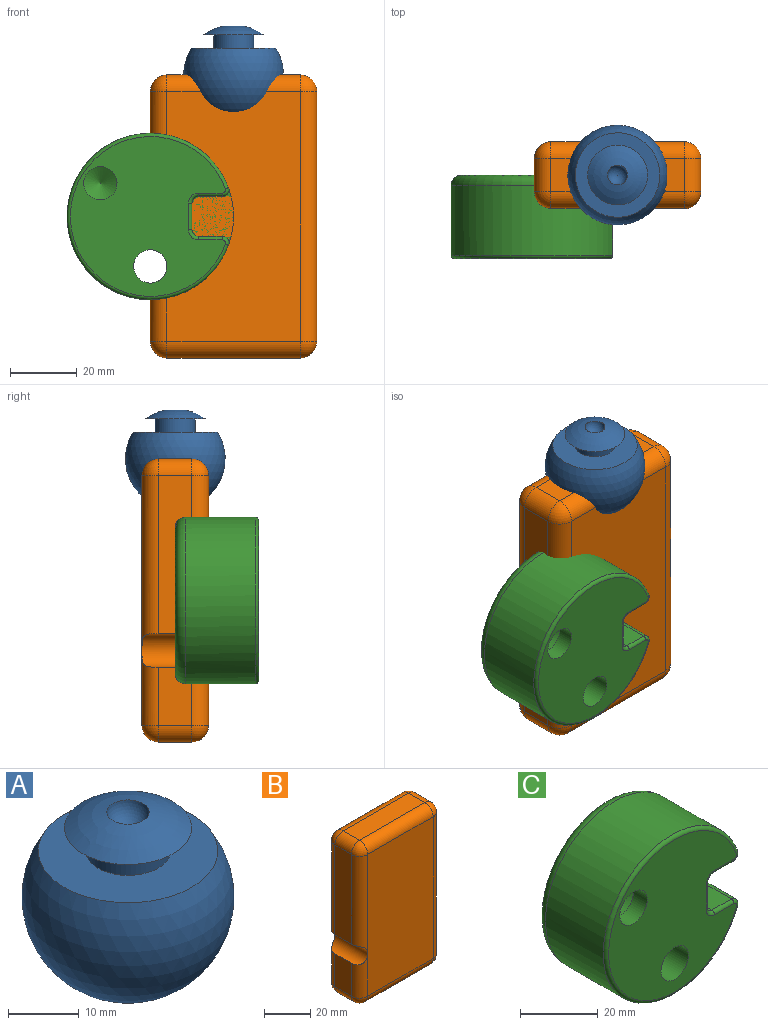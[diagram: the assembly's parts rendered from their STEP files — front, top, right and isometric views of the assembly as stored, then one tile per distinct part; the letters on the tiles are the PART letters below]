
ASSEMBLY  parts=3 mates=2
PART A: 6 faces, bbox 30x30x29.7 mm
  f0: sphere r=15mm, area 254.5mm2, adj f1,f4
  f1: sphere r=3mm, area 50.9mm2, adj f0
  f2: cylinder r=6mm len=12mm, axis (0,0,1), area 150.8mm2, adj f3,f4
  f3: plane 25.38x25.38mm, normal (0,0,1), area 392.7mm2, adj f2,f5
  f4: plane 18x18mm, normal (0,0,-1), area 141.4mm2, adj f0,f2
  f5: sphere r=15mm, area 2167.7mm2, adj f3
PART B: 30 faces, bbox 50x20x85 mm
  f0: plane 47.5x10mm, normal (-1,0,0), area 475mm2, adj f7,f8,f9,f25
  f1: plane 17.5x10mm, normal (-1,0,0), area 175mm2, adj f7,f12,f13,f17
  f2: plane 40x10mm, normal (0,0,-1), area 400mm2, adj f14,f17,f18,f21
  f3: plane 75x40mm, normal (0,1,0), area 3000mm2, adj f8,f10,f12,f21,f29
  f4: plane 40x10mm, normal (0,0,1), area 400mm2, adj f22,f25,f26,f29
  f5: plane 75x40mm, normal (0,-1,0), area 3000mm2, adj f9,f11,f13,f14,f22
  f6: plane 75x10mm, normal (1,0,0), area 750mm2, adj f10,f11,f18,f26
  f7: cylinder r=5mm len=20mm, axis (0,-1,0), area 291.5mm2, adj f0,f1,f8,f9,f12,f13
  f8: cylinder r=5mm len=52.5mm, axis (0,0,-1), area 378.7mm2, adj f0,f3,f7,f27
  f9: cylinder r=5mm len=52.5mm, axis (0,0,1), area 378.7mm2, adj f0,f5,f7,f23
  f10: cylinder r=5mm len=75mm, axis (0,0,1), area 589mm2, adj f3,f6,f20,f28
  f11: cylinder r=5mm len=75mm, axis (0,0,-1), area 589mm2, adj f5,f6,f16,f24
  f12: cylinder r=5mm len=22.5mm, axis (0,0,-1), area 143.1mm2, adj f1,f3,f7,f19
  f13: cylinder r=5mm len=22.5mm, axis (0,0,1), area 143.1mm2, adj f1,f5,f7,f15
  f14: cylinder r=5mm len=40mm, axis (1,0,0), area 314.2mm2, adj f2,f5,f15,f16
  f15: sphere r=5mm, area 39.3mm2, adj f13,f14,f17
  f16: sphere r=5mm, area 39.3mm2, adj f11,f14,f18
  f17: cylinder r=5mm len=10mm, axis (0,-1,0), area 78.5mm2, adj f1,f2,f15,f19
  f18: cylinder r=5mm len=10mm, axis (0,1,0), area 78.5mm2, adj f2,f6,f16,f20
  f19: sphere r=5mm, area 39.3mm2, adj f12,f17,f21
  f20: sphere r=5mm, area 39.3mm2, adj f10,f18,f21
  f21: cylinder r=5mm len=40mm, axis (-1,0,0), area 314.2mm2, adj f2,f3,f19,f20
  f22: cylinder r=5mm len=40mm, axis (-1,0,0), area 314.2mm2, adj f4,f5,f23,f24
  f23: sphere r=5mm, area 39.3mm2, adj f9,f22,f25
  f24: sphere r=5mm, area 39.3mm2, adj f11,f22,f26
  f25: cylinder r=5mm len=10mm, axis (0,1,0), area 78.5mm2, adj f0,f4,f23,f27
  f26: cylinder r=5mm len=10mm, axis (0,-1,0), area 78.5mm2, adj f4,f6,f24,f28
  f27: sphere r=5mm, area 39.3mm2, adj f8,f25,f29
  f28: sphere r=5mm, area 39.3mm2, adj f10,f26,f29
  f29: cylinder r=5mm len=40mm, axis (1,0,0), area 314.2mm2, adj f3,f4,f27,f28
PART C: 23 faces, bbox 54.1x25x54.1 mm
  f0: cylinder r=25mm len=50mm, axis (0,1,0), area 3050mm2, adj f6,f11,f13,f14,f15
  f1: plane 48x46.56mm, normal (0,-1,0), area 1485.3mm2, adj f4,f5,f15,f16,f17,f18,f19,f20
  f2: plane 44x44mm, normal (0,1,0), area 1442mm2, adj f5,f14
  f3: cone r=0mm half-angle=59deg, axis (0,-1,0), area 91.6mm2, adj f4
  f4: cylinder r=5mm len=10mm, axis (0,-1,0), area 157.1mm2, adj f1,f3
  f5: cylinder r=5mm len=25mm, axis (0,-1,0), area 785.4mm2, adj f1,f2
  f6: plane 17.39x12.5mm, normal (0,-1,0), area 148.9mm2, adj f0,f7,f8,f9,f10,f11,f12,f13
  f7: plane 14x8mm, normal (1,0,0), area 112mm2, adj f6,f10,f12,f22
  f8: plane 14x7.06mm, normal (0,0,1), area 98.9mm2, adj f6,f10,f11,f18
  f9: plane 14x7.06mm, normal (0,0,-1), area 98.9mm2, adj f6,f12,f13,f19
  f10: cylinder r=2mm len=14mm, axis (0,-1,0), area 44mm2, adj f6,f7,f8,f20
  f11: cylinder r=2mm len=14mm, axis (0,1,0), area 53.9mm2, adj f0,f6,f8,f16
  f12: cylinder r=2mm len=14mm, axis (0,1,0), area 44mm2, adj f6,f7,f9,f21
  f13: cylinder r=2mm len=14mm, axis (0,1,0), area 53.9mm2, adj f0,f6,f9,f17
  f14: torus R=22mm, axis (0,-1,0), area 707.9mm2, adj f0,f2
  f15: torus R=24mm, axis (0,-1,0), area 215.7mm2, adj f0,f1,f16,f17
  f16: torus R=1mm, axis (0,-1,0), area 5mm2, adj f1,f11,f15,f18
  f17: torus R=1mm, axis (0,-1,0), area 5mm2, adj f1,f13,f15,f19
  f18: cylinder r=1mm len=7.06mm, axis (-1,0,0), area 11.1mm2, adj f1,f8,f16,f20
  f19: cylinder r=1mm len=7.06mm, axis (1,0,0), area 11.1mm2, adj f1,f9,f17,f21
  f20: torus R=3mm, axis (0,-1,0), area 5.8mm2, adj f1,f10,f18,f22
  f21: torus R=3mm, axis (0,-1,0), area 5.8mm2, adj f1,f12,f19,f22
  f22: cylinder r=1mm len=8mm, axis (0,0,1), area 12.6mm2, adj f1,f7,f20,f21
PLACE A t=(-2.31,0.6,44.98)mm
PLACE B t=(-27.31,0.6,2.48)mm
PLACE C t=(-27.31,0.6,2.48)mm
MATE ball A.f2 <-> B.f4  axis (0,0,1) through (-2.31,0.6,44.98)mm
MATE fastened B.f7 <-> C.f5  axis (0,-1,0) through (-27.31,0.6,-12.52)mm
